# Revit family: Zumtobel EXENEO S
name_source: partatom
category: Lighting Fixtures
revit_build: Autodesk Revit 2018 (Build: 20170223_1515(x64)
units: mm (PartAtom-declared; Revit-internal decimal feet)

## family parameters
Cut with Voids When Loaded = No
Host = Face
Light Source = Yes
OmniClass Number = 23.80.70.11
OmniClass Title = Luminaries for Internal Lighting
Part Type = Normal
Room Calculation Point = No
Round Connector Dimension = Use Diameter
Shared = No

## types (1)
- EXENEO S 4800-750 CL MB M20M EX1/21
    Apparent Load = 44 VA
    Assembly Code = D5020200
    Body = ZG_Metal_Black
    Color Filter = 16777215
    Default Elevation = 0 mm  [stored 0 ft]
    Description = Explosion-proof LED moisture-proof diffuser luminaire
    Dimming Lamp Color Temperature Shift = <None>
    Emit Shape Visible in Rendering = Yes
    Emit from Rectangle Length = 275 mm
    Emit from Rectangle Width = 141 mm
    Height = 115 mm
    Lamp = LED
    Length = 770 mm
    Manufacturer = Zumtobel Lighting
    Model = 42188147
    Photometric Web File = 42188147_(STD_LEO).IES
    Reflector = ZG_Metal_White_Self_Illumination
    Tilt Angle = -90.00°
    URL = http://www.zumtobel.com
    Voltage = 230 V
    Width = 201 mm

note: [stored X ft] marks values corroborated as IEEE doubles in the binary element streams (Revit-internal decimal feet)

## geometry (parser evidence)
native form markers: Sweep x2
no freeform markers — native parametric forms only
